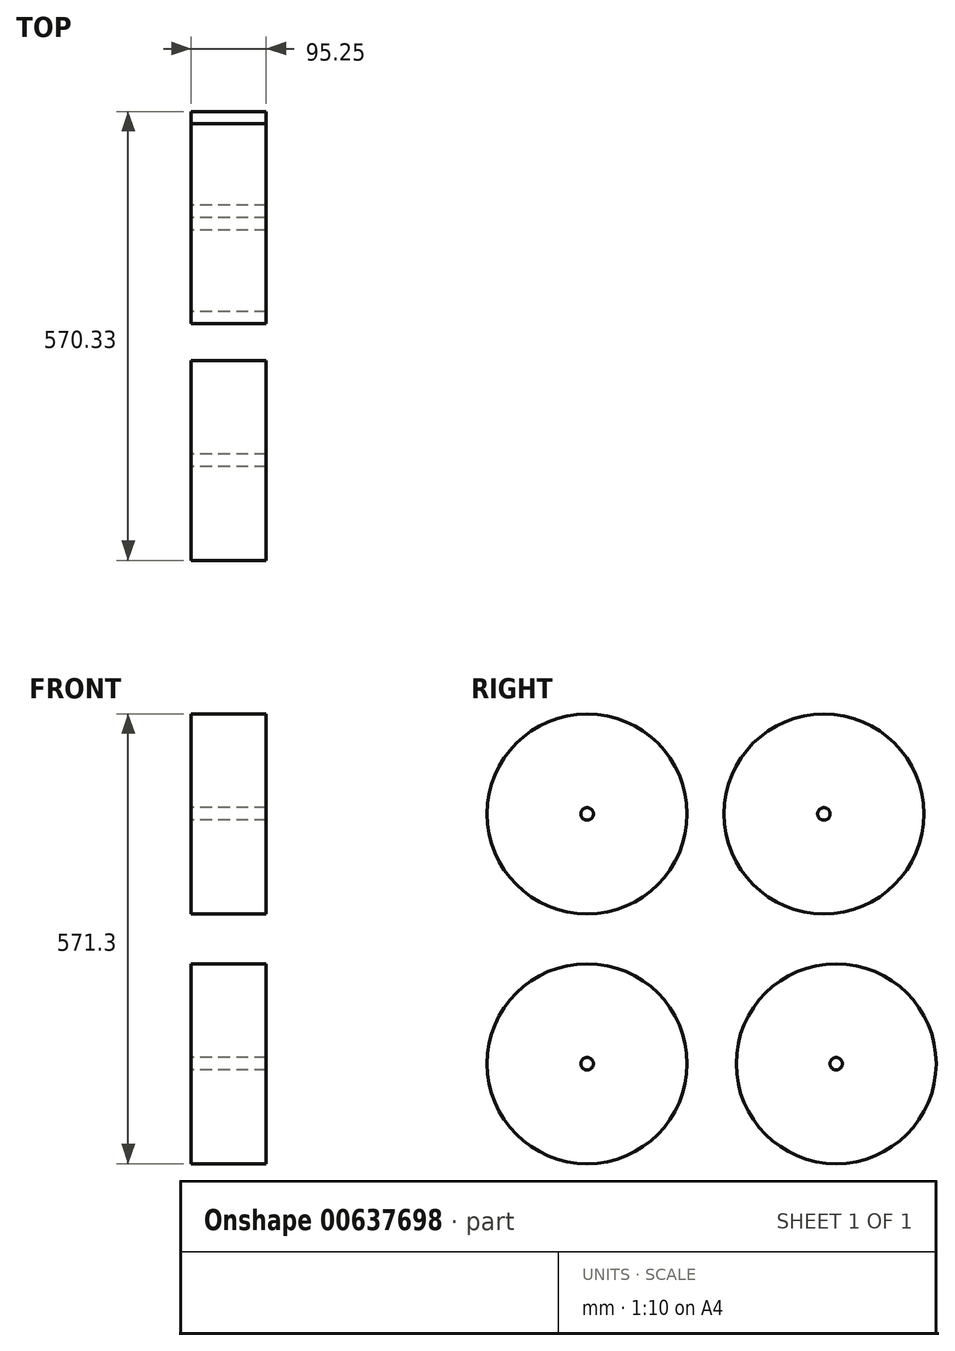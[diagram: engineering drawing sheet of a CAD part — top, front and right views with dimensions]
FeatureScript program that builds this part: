
annotation { "Feature Type Name" : "Feature", "Feature Type Description" : "" }
export const myFeature = defineFeature(function(context is Context, id is Id, definition is map)
    precondition{}
    {
        {
            var Q0;
            Q0=qCreatedBy(makeId("Right.planeOp"),FACE);
            var sketch = newSketch(context, id + "F0", { "sketchPlane" : qUnion([Q0])});
            skCircle(sketch, "E0", {"center": v(-42.4, 44.35) * mm, "radius": 127 * mm});
            skCircle(sketch, "E1", {"center": v(258.3, 44.35) * mm, "radius": 127 * mm});
            skCircle(sketch, "E2", {"center": v(-42.4, -272.95) * mm, "radius": 127 * mm});
            skCircle(sketch, "E3", {"center": v(273.93, -272.95) * mm, "radius": 127 * mm});
            skLineSegment(sketch, "E4", {"start": v(84.6, 44.35) * mm, "end": v(-169.4, 44.35) * mm, "construction": true});
            skCircle(sketch, "E5", {"center": v(-42.4, 44.35) * mm, "radius": 7.94 * mm});
            skCircle(sketch, "E6", {"center": v(258.3, 44.35) * mm, "radius": 7.94 * mm});
            skCircle(sketch, "E7", {"center": v(-42.4, -272.95) * mm, "radius": 7.94 * mm});
            skCircle(sketch, "E8", {"center": v(273.93, -272.95) * mm, "radius": 7.94 * mm});
            skSolve(sketch);
        }
        {
            var Q0;
            Q0=makeQuery(id+"F0.imprint","IMPRINT",FACE,{"disambiguationData":[TD([[makeQuery(id+"F0.imprint","IMPRINT",EDGE,{"derivedFrom":sQuery(id+"F0.wireOp",EDGE,"E0")}),1.0]])]});
            var Q1;
            Q1=makeQuery(id+"F0.imprint","IMPRINT",FACE,{"disambiguationData":[TD([[makeQuery(id+"F0.imprint","IMPRINT",EDGE,{"derivedFrom":sQuery(id+"F0.wireOp",EDGE,"E1")}),1.0]])]});
            var Q2;
            Q2=makeQuery(id+"F0.imprint","IMPRINT",FACE,{"disambiguationData":[TD([[makeQuery(id+"F0.imprint","IMPRINT",EDGE,{"derivedFrom":sQuery(id+"F0.wireOp",EDGE,"E3")}),1.0]])]});
            var Q3;
            Q3=makeQuery(id+"F0.imprint","IMPRINT",FACE,{"disambiguationData":[TD([[makeQuery(id+"F0.imprint","IMPRINT",EDGE,{"derivedFrom":sQuery(id+"F0.wireOp",EDGE,"E2")}),1.0]])]});
            extrude(context, id + "F1", {"entities" : qUnion([Q0, Q1, Q2, Q3]), "depth" : 95.25 * mm, "offsetDistance" : 25.4 * mm});
        }
    });
